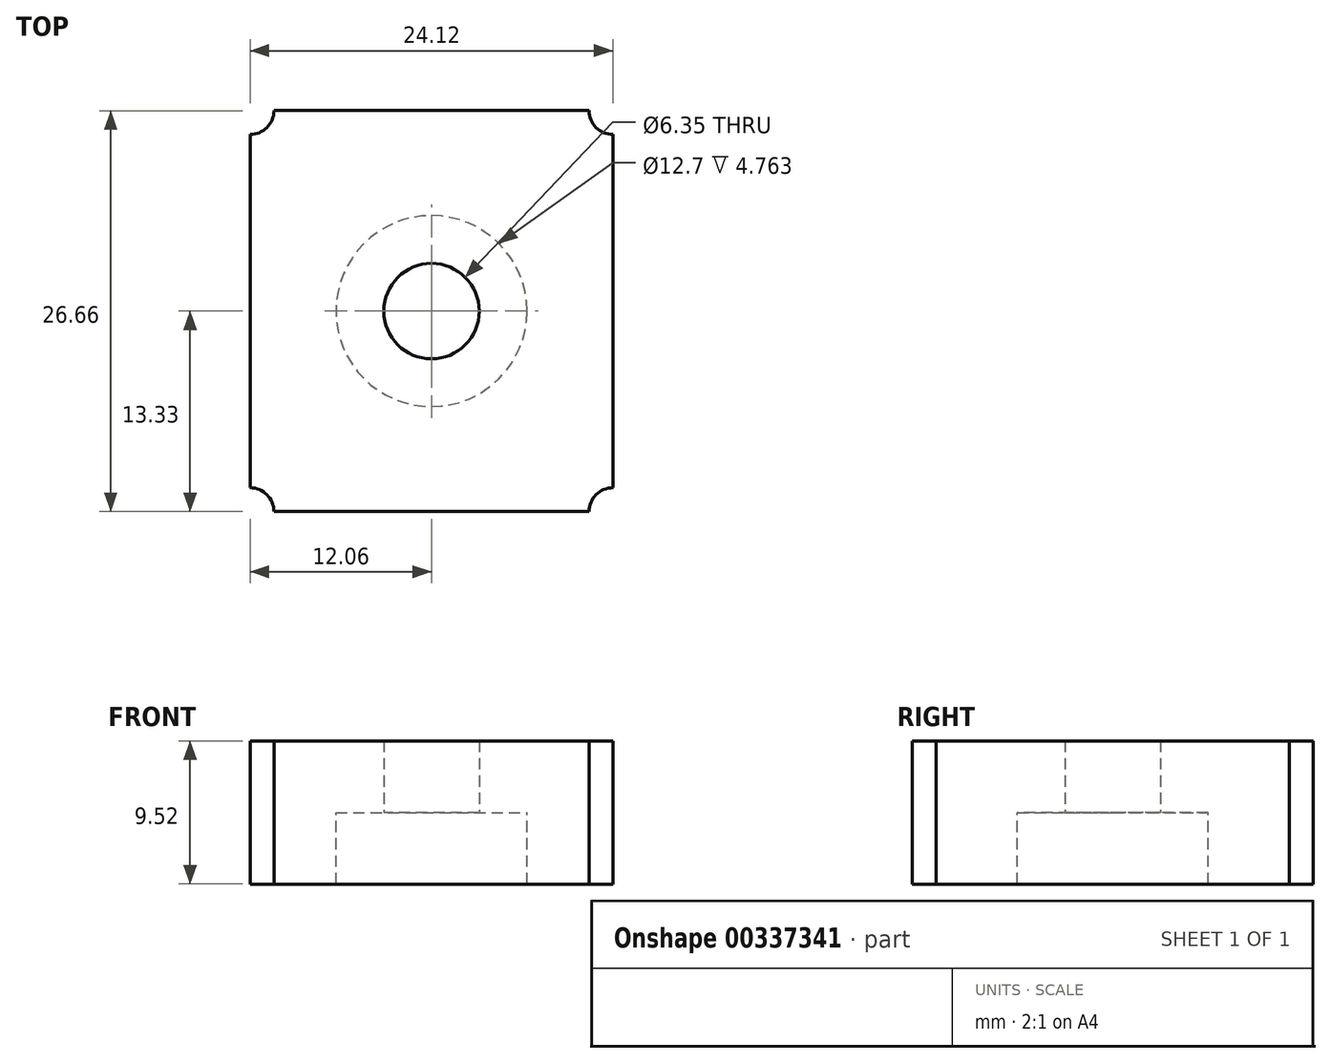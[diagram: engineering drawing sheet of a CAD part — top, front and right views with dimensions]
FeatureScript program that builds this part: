
annotation { "Feature Type Name" : "Feature", "Feature Type Description" : "" }
export const myFeature = defineFeature(function(context is Context, id is Id, definition is map)
    precondition{}
    {
        {
            var Q0;
            Q0=qCreatedBy(makeId("Top.planeOp"),FACE);
            var sketch = newSketch(context, id + "F0", { "sketchPlane" : qUnion([Q0])});
            skLineSegment(sketch, "E0.bottom", {"start": v(12.07, 13.34) * mm, "end": v(-12.06, 13.34) * mm});
            skLineSegment(sketch, "E0.top", {"start": v(12.06, -13.34) * mm, "end": v(-12.07, -13.34) * mm});
            skLineSegment(sketch, "E0.left", {"start": v(12.07, 13.34) * mm, "end": v(12.07, -13.34) * mm});
            skLineSegment(sketch, "E0.right", {"start": v(-12.06, 13.34) * mm, "end": v(-12.07, -13.34) * mm});
            skPoint(sketch, "E0.middle", {"position": v(0, 0) * mm});
            skCircle(sketch, "E1", {"center": v(-12.07, -13.34) * mm, "radius": 1.59 * mm});
            skCircle(sketch, "E2", {"center": v(12.06, -13.34) * mm, "radius": 1.59 * mm});
            skCircle(sketch, "E3", {"center": v(12.07, 13.34) * mm, "radius": 1.59 * mm});
            skCircle(sketch, "E4", {"center": v(-12.06, 13.34) * mm, "radius": 1.59 * mm});
            skCircle(sketch, "E5", {"center": v(0, 0) * mm, "radius": 3.18 * mm});
            skSolve(sketch);
        }
        {
            var Q0;
            Q0=makeQuery(id+"F0.imprint","IMPRINT",FACE,{"disambiguationData":[TD([[makeQuery(id+"F0.imprint","IMPRINT",EDGE,{"derivedFrom":sQuery(id+"F0.wireOp",EDGE,"E5")}),-1.0]])]});
            extrude(context, id + "F1", {"entities" : qUnion([Q0]), "depth" : 4.76 * mm});
        }
        {
            var Q0;
            Q0=makeQuery(id+"F1.opExtrude","CAP_FACE",FACE,{"disambiguationData":[OSD([sQuery(id+"F0.wireOp",EDGE,"E0.bottom"),sQuery(id+"F0.wireOp",EDGE,"E0.top"),sQuery(id+"F0.wireOp",EDGE,"E0.left"),sQuery(id+"F0.wireOp",EDGE,"E0.right"),sQuery(id+"F0.wireOp",EDGE,"E1"),sQuery(id+"F0.wireOp",EDGE,"E2"),sQuery(id+"F0.wireOp",EDGE,"E3"),sQuery(id+"F0.wireOp",EDGE,"E4"),sQuery(id+"F0.wireOp",EDGE,"E5")])],"isStart":true});
            var sketch = newSketch(context, id + "F2", { "sketchPlane" : qUnion([Q0])});
            skCircle(sketch, "E6", {"center": v(0, 0) * mm, "radius": 6.35 * mm});
            skSolve(sketch);
        }
        {
            var Q0;
            Q0=makeQuery(id+"F2.imprint","IMPRINT",FACE,{"disambiguationData":[TD([[makeQuery(id+"F2.imprint","IMPRINT",EDGE,{"derivedFrom":sQuery(id+"F2.wireOp",EDGE,"E6")}),-1.0]])]});
            extrude(context, id + "F3", {"entities" : qUnion([Q0]), "operationType" : NewBodyOperationType.ADD, "depth" : 4.76 * mm});
        }
    });
